# Revit family: Franke_Flavor_Station_FS3-A600_FM_EC_A600_FM_CM_A800_FM_EC(EU,CH,GB)
name_source: partatom
category: Specialty Equipment
revit_build: Autodesk Revit 2015 (Build: 20140606_1530(x64)
units: mm (PartAtom-declared; Revit-internal decimal feet)

## types (2) — shared parameters
Assembly Code = key module Flavor Station
Capacity = up to 3 bottles
Cycle = 50 Hz
Cycle Alternative = 60 Hz
Depth (mm) = 452 mm  [stored 1.48294 ft]
Description = key module Flavor Station enables the automated and constant dosing of syrup in the coffee / milk
Energy loss acc. to DIN 18873 = -
Height (mm) = 544 mm
Keynote = key module Flavor Station
Manufacturer = Franke
Max Overcurrent Protection = -
Model = 410888 - Flavor Station FS3-A600 FM EC, A600 FM CM, A800 FM EC
Number of Nutral Conductors = 1
Number of Poles = 1
Number of Protective Conductors = 1
URL = https://www.franke.com
Volts max. = 240 V
Volts min. = 220 V
Watts max. = 0 W
Watts min. = 0 W
Weight = 17 kg
Width (mm) = 200 mm  [stored 0.656168 ft]
zero-valued in all types: Cost

## per-type parameters (varying)
| type | Frontcover |
| Flavor Station FS3-A600 FM EC,A600 FM CM,A800 FM EC(220-240V/black line/EU,CH,GB) | Franke Black |
| Flavor Station FS3-A600 FM EC,A600 FM CM,A800 FM EC(220-240V/anthracite/EU,CH,GB) | Franke Anthracite |

note: [stored X ft] marks values corroborated as IEEE doubles in the binary element streams (Revit-internal decimal feet)
